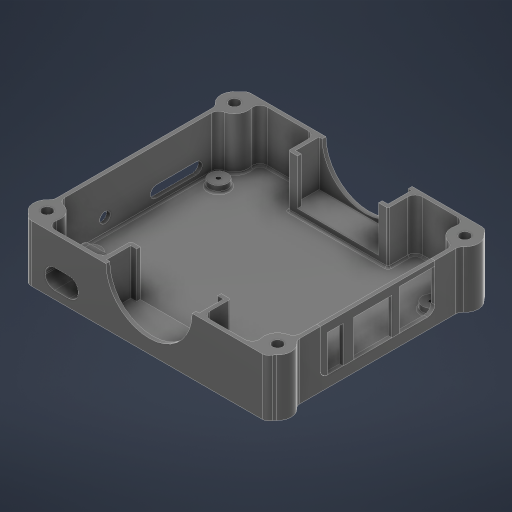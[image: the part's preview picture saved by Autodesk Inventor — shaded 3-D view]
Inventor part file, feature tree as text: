
AUTODESK INVENTOR PART (.ipt)
format: ipt  version: 2023 (Build 270158000, 158)  size: 1,126,912 bytes
history: native  units: in
note: dims shown in document units (in); Inventor stores cm internally (conversion verified against a paired STEP export)
features: sketch x21, extrude x19, reference x14, projected_geometry x11, other x5, plane x3, fillet x3, hole x2
ambient origin geometry x8: Origin, YZ Plane, XZ Plane, XY Plane, X Axis, Y Axis, Z Axis, Center Point
bodies: Solid1 (feature_tree), Solid2 (feature_tree), Solid3 (feature_tree), Solid4 (feature_tree)
feature tree (78):
  plane  "Work Plane1"
  extrude  "Extrusion1"  Depth=0.04in
  extrude  "Extrusion2"  Depth=0.5512in
  extrude  "Extrusion3"  Depth=0.065in
  extrude  "Extrusion4"  TaperAngle=0.0deg  [1 undecoded]
  extrude  "Extrusion5"  Depth=0.7874in TaperAngle=0.0deg
  extrude  "Extrusion6"  Depth=0.0787in TaperAngle=0.0deg
  sketch  "Sketch7"  dims[d16=0.1in d17=0.1181in d18=0.0in]
  plane  "Work Plane2"
  extrude  "Extrusion7"  Depth=0.1181in TaperAngle=0.0deg
  extrude  "Extrusion8"  Depth=0.1181in TaperAngle=0.0deg
  extrude  "Extrusion9"  Depth=0.1181in TaperAngle=0.0deg
  sketch  "Sketch10"  dims[d28=1.7853in d29=0.05in]
  plane  "Work Plane3"
  extrude  "Extrusion10"  Depth=0.05in
  extrude  "Extrusion11"  Depth=0.05in
  extrude  "Extrusion12"  Depth=0.8661in
  hole  "Hole1"  [1 undecoded]
  extrude  "Extrusion13"  Depth=0.1in
  fillet  "Fillet1"  Radius=0.1in
  extrude  "Extrusion14"  Depth=0.063in
  fillet  "Fillet2"  Radius=0.063in
  hole  "Hole2"  [1 undecoded]
  fillet  "Fillet3"  Radius=1.0in
  extrude  "Extrusion15"  Depth=1.7323in
  extrude  "Extrusion16"  Depth=1.0in TaperAngle=0.0deg
  extrude  "Extrusion17"  Depth=0.1in
  extrude  "Extrusion18"  Depth=0.063in
  extrude  "Extrusion19"  Depth=0.1in
  sketch  "Sketch1"  dims[d0=0.04in d1=0.04in]
  reference  "Reference1"
  reference  "Reference2"
  sketch  "Sketch2"  dims[d2=0.5512in d3=0.5512in]
  projected_geometry  "Projected Loop1"
  sketch  "Sketch3"  dims[d5=0.065in d6=0.065in]
  sketch  "Sketch4"  dims[d7=0.065in d8=0.0in]
  reference  "Reference3"
  reference  "Reference4"
  reference  "Reference5"
  reference  "Reference6"
  sketch  "Sketch5"  dims[d9=0.065in d10=0.7874in d11=0.0in]
  reference  "Reference7"
  reference  "Reference8"
  reference  "Reference9"
  sketch  "Sketch6"  dims[d12=0.1969in d13=0.0in d14=0.0787in d15=0.0in]
  reference  "Reference10"
  reference  "Reference11"
  sketch  "Sketch8"  dims[d19=0.6378in d22=0.1181in d23=0.0in]
  projected_geometry  "Projected Loop2"
  sketch  "Sketch9"  dims[d24=0.05in d25=0.1181in d26=0.0in]
  sketch  "Sketch11"  dims[d30=0.15in d31=0.05in]
  sketch  "Sketch12"  dims[d32=1.7323in d33=0.8661in]
  sketch  "Sketch13"  dims[d34=0.4843in d35=1.0in d36=0.0in]
  sketch  "Sketch14"  dims[d45=1.0in d46=0.0in d47=0.1in d48=0.1in]
  projected_geometry  "Projected Loop3"
  projected_geometry  "Projected Loop4"
  sketch  "Sketch15"  dims[d49=0.063in d50=0.063in d51=0.063in]
  sketch  "Sketch17"  dims[d52=0.063in d53=1.4961in d54=1.0in d55=0.0in]
  sketch  "Sketch18"  dims[d56=0.4724in d57=1.7323in]
  projected_geometry  "Projected Loop5"
  sketch  "Sketch19"  dims[d58=0.8661in d59=1.0in d60=0.0in]
  projected_geometry  "Projected Loop6"
  sketch  "Sketch20"  dims[d62=0.063in d63=0.1in]
  projected_geometry  "Projected Loop7"
  projected_geometry  "Projected Loop8"
  projected_geometry  "Projected Loop9"
  projected_geometry  "Projected Loop10"
  sketch  "Sketch21"  dims[d64=0.063in d65=0.063in]
  projected_geometry  "Projected Loop11"
  sketch  "Sketch22"  dims[d66=0.063in d67=0.1in d68=1.0in d69=0.0in d70=1.4961in d71=1.0in d72=0.0in d73=0.0793in d74=0.197in d75=0.173in d76=0.079in d77=0.5635in d78=1.0in d79=0.8108in d80=0.0394in d81=0.625in d82=0.0in d83=0.125in d84=3.25in d85=4.0in d86=0.4724in d87=0.1969in d88=0.0in d89=0.125in d90=0.177in d91=0.75in d92=0.313in d93=0.75in d94=0.5635in d95=1.0in d96=0.8108in d97=0.0312in d98=0.0079in d99=0.0in d100=0.0079in d101=0.0in d102=0.0079in d103=0.0in d104=0.0079in d105=0.0in d106=0.1875in d107=1.0in d108=0.0in]
  reference  "Reference12"
  reference  "Reference13"
  reference  "Reference14"
  other  "OrangePICover.iam"
  other  "OPi5_pcb_asm-0809:1"
  other  "orangepicover-002:1"
  other  "OPi5_pcb_asm-0809:2"
  other  "Assembly10"
note: 3 required parameter values undecoded (feature->parameter linkage not recoverable at this tier; creation-order binding heuristic only, values carry confidence <= 0.55)
